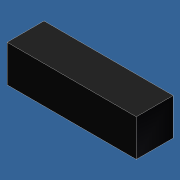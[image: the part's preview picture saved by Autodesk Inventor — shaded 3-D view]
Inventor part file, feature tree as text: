
AUTODESK INVENTOR PART (.ipt)
format: ipt  version: unknown  size: 166,400 bytes
history: native  units: mm
features: extrude x1, sketch x1
ambient origin geometry x8: Origin, YZ Plane, XZ Plane, XY Plane, X Axis, Y Axis, Z Axis, Center Point
feature tree (2):
  extrude  "Выдавливание2"  Depth=3.5mm
  sketch  "Эскиз2"
